# Revit family: R-MBD-268
name_source: partatom
category: Portes
units: mm (PartAtom-declared; Revit-internal decimal feet)

## family parameters
Couper avec des vides une fois chargée = Non
Hôte = Mur
Partagée = Non
Point de calcul de pièce = Oui
Toujours verticalement = Non

## types (1)
- MBD-268
    ----- PARAMETRES DE L'HÔTE -------------------- = .
    ----- PARAMETRES DES VANTAUX -------------------- = .
    ----- PARAMETRES POSITION HUISSERIE -------------------- = .
    ----- PARAMETRES PROFIL -------------------- = .
    ----- TYPE D'HUISSERIE -------------------- = .
    ----- TYPE DE VANTAIL -------------------- = .
    --------- EQUIPEMENTS ----------------- = .
    1 Vantail = Non
    2 Vantaux = Oui
    Certification = D.A.S. Mode 2 certifié NF
    Code_MAJ = 2301270102MBD268
    Coloris Oculus = Lauan - Meranti
    Coloris Oculus Métal = Acier - finition peinture thermolaque - gris - brillant
    Coloris protection parement PVC = Acrylique
    Coloris_Chants = BER
    Construction analytique = <Aucun>
    DAS = Oui
    Description = Bloc-porte bois D.A.S. 2 vantaux SP51 avec ferme-portes DORMA et battement feuilluré, simple action, EI60, D.A.S. certifié NF, sur huisserie PROFEU HOSPITALIER
    Décalage_Largeur_Profil = 18 mm  [stored 0.0590551 ft]
    Décalage_Profondeur_Profil = 0 mm  [stored 0 ft]
    Décalage_Seuil_Vantail = 0 mm  [stored 0 ft]
    Désaffleurement_Vantail = 0 mm  [stored 0 ft]
    Ep_Tôle_Profil = 2 mm  [stored 0.00656168 ft]
    Epaisseurs_Vantaux = 51 mm
    Espacement_Paumelle_Vantail = 0 mm  [stored 0 ft]
    FDES Inies = https://www.base-inies.fr
    Fabricant = MALERBA
    Ferrage_Encastre = Non
    Feuillure_Basse_Vantail = Non
    Fiche_Produit = MBD-268
    Hauteur Feuillure Basse Vantail = 15 mm  [stored 0.0492126 ft]
    Hauteur protection parement PVC = 600 mm  [stored 1.9685 ft]
    Hauteur_Axe_Bequille = 1045 mm  [stored 3.42848 ft]
    Hauteur_Vantaux_Souhaitée = 2040 mm  [stored 6.69291 ft]
    Ht Microviseur = 1500 mm  [stored 4.92126 ft]
    Huisserie_Bati_d'Angle = Non
    Huisserie_HB_Banches = Non
    Huisserie_HT_RV_Avec_contre_Feuillure = Non
    Huisserie_HT_RV_Sans_contre_Feuillure = Oui
    Huisserie_Reprise_de_Doublage = Non
    Inv_Espacement_Paumelle_Vantail = 10 mm  [stored 0.0328084 ft]
    Inv_Position_Largeur_Paumelle = 10 mm  [stored 0.0328084 ft]
    Jeu Profondeur Recouvrement Vantail = 0 mm  [stored 0 ft]
    Jeu_1 = 0 mm  [stored 0 ft]
    Jeu_2 = 0 mm  [stored 0 ft]
    Jeu_Côté_Articulation_Vantail = 2 mm  [stored 0.00656168 ft]
    Jeu_Côté_Fermeture_Vantail = 3 mm  [stored 0.00984252 ft]
    Jeu_Haut = 0 mm  [stored 0 ft]
    Jeu_Traverse_Basse_Vantail = 5 mm  [stored 0.0164042 ft]
    Jeu_Traverse_Haute_Vantail = 3 mm  [stored 0.00984252 ft]
    Largeur Feuillure Battement Articulation = 15 mm  [stored 0.0492126 ft]
    Largeur_Axe_Bequille = 50 mm  [stored 0.164042 ft]
    Largeur_Contre_Feuillure_Profil = 22 mm  [stored 0.0721785 ft]
    Largeur_Feuillure_Battement_Semi_Fixe = 15 mm  [stored 0.0492126 ft]
    Largeur_Feuillure_Battement_Service = 15 mm  [stored 0.0492126 ft]
    Largeur_Feuillure_Profil = 18 mm  [stored 0.0590551 ft]
    Largeur_Feuillure_hôte_coté_opposé = 0 mm  [stored 0 ft]
    Largeur_Feuillure_hôte_coté_ouvrant = 0 mm  [stored 0 ft]
    Largeur_Parement_coté_Feuillure_Profil = 40 mm  [stored 0.131234 ft]
    Largeur_Parement_coté_opposé_Feuillure_Profil = 58 mm  [stored 0.190289 ft]
    Largeur_Vantail_Semi_Fixe_Souhaitée = 630 mm  [stored 2.06693 ft]
    Largeur_Vantail_Service_Souhaitée = 930 mm  [stored 3.05118 ft]
    Materiau_Scellement = <Par catégorie>
    Materiaux_Dominant = Bois
    Maternelle = Non
    Microviseur = Non
    Modèle = 53-SA-HM
    Nombre_Vantaux = 2
    Note d'identification = 2V SP51 DAS - FP DORMA - FEUILLURE - PROFEU HOSPITALIER
    Paumelle 5 inversée = Non
    Paumelle_1 = 230 mm  [stored 0.754593 ft]
    Paumelle_2 = 809 mm  [stored 2.6542 ft]
    Paumelle_3 = 809 mm  [stored 2.6542 ft]
    Paumelle_4 = 165 mm
    Paumelle_5 inversée = 165 mm
    Position_Largeur_Paumelle = 5 mm  [stored 0.0164042 ft]
    Profondeur Feuillure Basse Vantail = 25 mm  [stored 0.082021 ft]
    Profondeur Feuillure Battement Articulation = 26 mm
    Profondeur_Contre_Feuillure_Profil = 28 mm
    Profondeur_Feuillure_Battement_Semi_Fixe = 41 mm  [stored 0.134514 ft]
    Profondeur_Feuillure_Battement_Service = 15 mm  [stored 0.0492126 ft]
    Profondeur_Feuillure_Profil = 60 mm  [stored 0.19685 ft]
    Profondeur_Feuillure_hôte_coté_opposé = 0 mm  [stored 0 ft]
    Profondeur_Feuillure_hôte_coté_ouvrant = 0 mm  [stored 0 ft]
    Profondeur_Retour_Parement_Profil = 3 mm  [stored 0.00984252 ft]
    Profondeur_Totale_Pose_Tunnel_Profil = 90 mm  [stored 0.295276 ft]
    Protection de parement PVC coté opposé aux paumelles = Non
    Protection de parement pvc côté paumelles = Non
    Reference_Commerciale = 2V SP51 FP
    Reprise_Doublage_1 = 0 mm  [stored 0 ft]
    Reprise_Doublage_2 = 0 mm  [stored 0 ft]
    Reprise_Doublage_Haut = 0 mm  [stored 0 ft]
    Resistance_Feu = EI60
    Schéma de simplification = S4
    Sens_Feu = Recto / Verso
    Thermique (W/m2.°K) = 0
    URL = https://www.malerba.fr
    Visibilite_Paum-4 = Oui
    Visibilite_Poignee = Oui

note: [stored X ft] marks values corroborated as IEEE doubles in the binary element streams (Revit-internal decimal feet)

## geometry (parser evidence)
native form markers: Blend x14
no freeform markers — native parametric forms only
